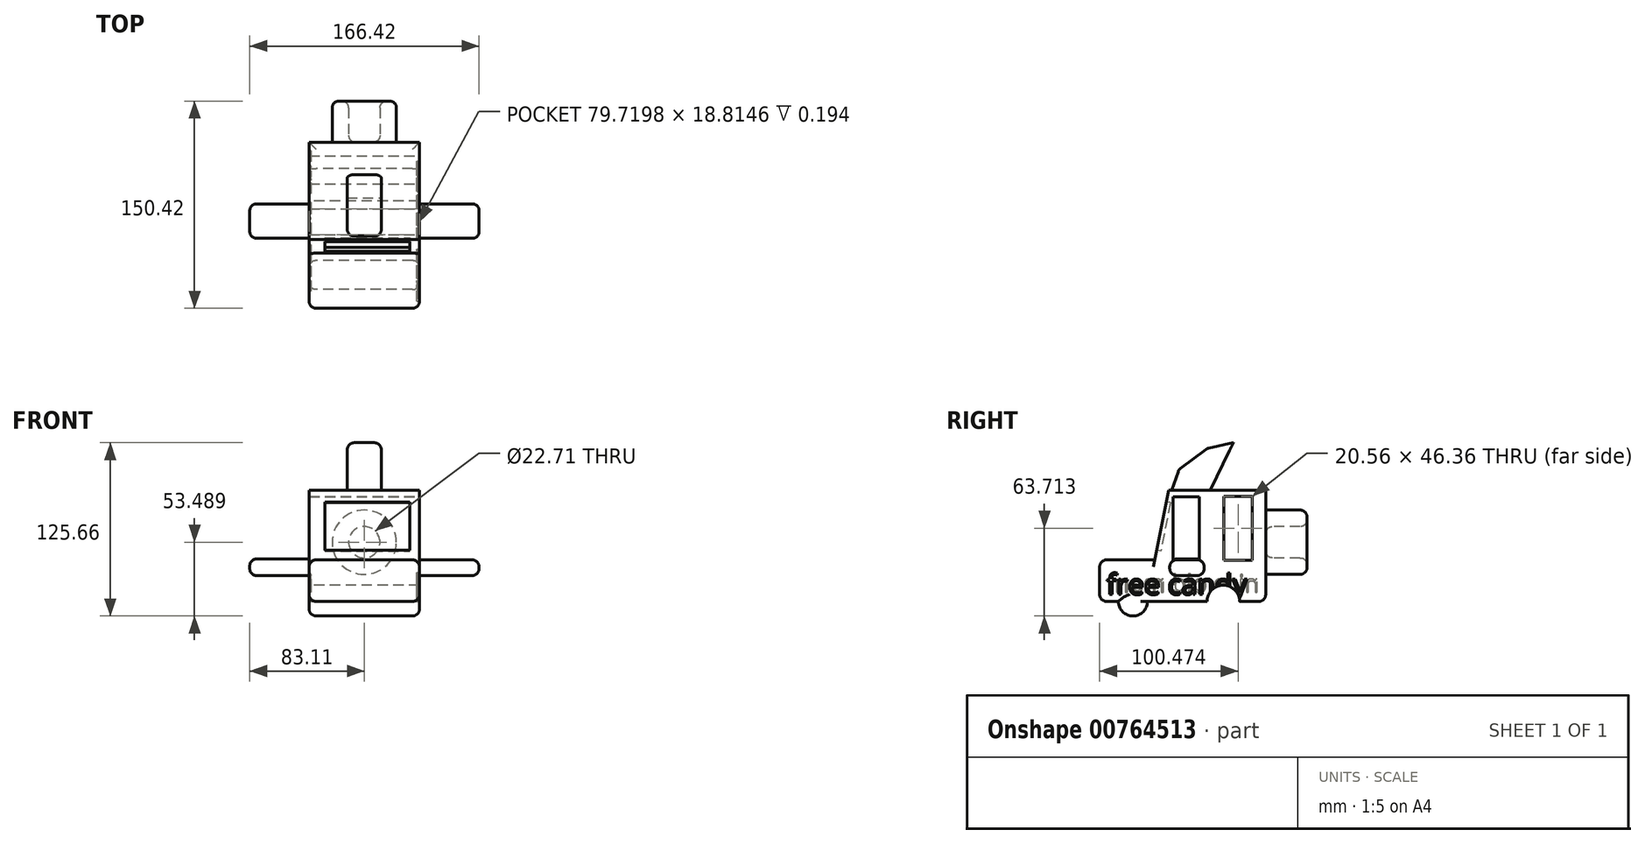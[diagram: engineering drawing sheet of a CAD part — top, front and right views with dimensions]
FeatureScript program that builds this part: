
annotation { "Feature Type Name" : "Feature", "Feature Type Description" : "" }
export const myFeature = defineFeature(function(context is Context, id is Id, definition is map)
    precondition{}
    {
        {
            var Q0;
            Q0=qCreatedBy(makeId("Right.planeOp"),FACE);
            var sketch = newSketch(context, id + "F0", { "sketchPlane" : qUnion([Q0])});
            skLineSegment(sketch, "E0", {"start": v(57.1, 32.48) * mm, "end": v(57.1, -48.17) * mm});
            skLineSegment(sketch, "E1", {"start": v(57.1, -48.17) * mm, "end": v(-63.33, -48.17) * mm});
            skLineSegment(sketch, "E2", {"start": v(-63.33, -48.17) * mm, "end": v(-63.33, -18) * mm});
            skLineSegment(sketch, "E3", {"start": v(-63.33, -18) * mm, "end": v(-23.28, -18) * mm});
            skLineSegment(sketch, "E4", {"start": v(57.1, 32.48) * mm, "end": v(-13.4, 32.48) * mm});
            skLineSegment(sketch, "E5", {"start": v(-13.4, 32.48) * mm, "end": v(-23.28, -18) * mm});
            skCircle(sketch, "E6", {"center": v(-39.2, -48.17) * mm, "radius": 10.5 * mm});
            skCircle(sketch, "E7", {"center": v(26.37, -48.17) * mm, "radius": 11.8 * mm});
            skSolve(sketch);
        }
        {
            var Q0;
            {var subQ5=sQuery(id+"F0.wireOp",EDGE,"E0");Q0=makeQuery(id+"F0.imprint","IMPRINT",FACE,{"disambiguationData":[TD([[makeQuery(id+"F0.imprint","IMPRINT",EDGE,{"derivedFrom":subQ5}),-1.0]])]});}
            extrude(context, id + "F1", {"entities" : qUnion([Q0]), "endBound" : BoundingType.SYMMETRIC, "depth" : 80 * mm, "offsetDistance" : 25 * mm});
        }
        {
            var Q0;
            {var subQ0=sQuery(id+"F0.wireOp",EDGE,"E6");var subQ1=sQuery(id+"F0.wireOp",EDGE,"E1");var subQ2=makeQuery(id+"F0.imprint","INTERSECT",VERTEX,{"disambiguationData":[OD(0.0)],"derivedFrom":[subQ1,subQ0]});Q0=makeQuery(id+"F0.imprint","IMPRINT",FACE,{"disambiguationData":[TD([[makeQuery(id+"F0.imprint","IMPRINT",EDGE,{"disambiguationData":[TD([[subQ2,-1.0]])],"derivedFrom":subQ1}),1.0]])]});}
            var Q1;
            {var subQ0=sQuery(id+"F0.wireOp",EDGE,"E6");var subQ1=sQuery(id+"F0.wireOp",EDGE,"E1");var subQ2=makeQuery(id+"F0.imprint","INTERSECT",VERTEX,{"disambiguationData":[OD(0.0)],"derivedFrom":[subQ1,subQ0]});Q1=makeQuery(id+"F0.imprint","IMPRINT",FACE,{"disambiguationData":[TD([[makeQuery(id+"F0.imprint","IMPRINT",EDGE,{"disambiguationData":[TD([[subQ2,-1.0]])],"derivedFrom":subQ1}),-1.0]])]});}
            var Q2;
            {var subQ0=sQuery(id+"F0.wireOp",EDGE,"E7");var subQ1=sQuery(id+"F0.wireOp",EDGE,"E1");var subQ2=makeQuery(id+"F0.imprint","INTERSECT",VERTEX,{"disambiguationData":[OD(0.0)],"derivedFrom":[subQ1,subQ0]});Q2=makeQuery(id+"F0.imprint","IMPRINT",FACE,{"disambiguationData":[TD([[makeQuery(id+"F0.imprint","IMPRINT",EDGE,{"disambiguationData":[TD([[subQ2,-1.0]])],"derivedFrom":subQ1}),1.0]])]});}
            var Q3;
            {var subQ0=sQuery(id+"F0.wireOp",EDGE,"E7");var subQ1=sQuery(id+"F0.wireOp",EDGE,"E1");var subQ2=makeQuery(id+"F0.imprint","INTERSECT",VERTEX,{"disambiguationData":[OD(0.0)],"derivedFrom":[subQ1,subQ0]});Q3=makeQuery(id+"F0.imprint","IMPRINT",FACE,{"disambiguationData":[TD([[makeQuery(id+"F0.imprint","IMPRINT",EDGE,{"disambiguationData":[TD([[subQ2,-1.0]])],"derivedFrom":subQ1}),-1.0]])]});}
            extrude(context, id + "F2", {"entities" : qUnion([Q0, Q1, Q2, Q3]), "operationType" : NewBodyOperationType.ADD, "endBound" : BoundingType.SYMMETRIC, "depth" : 80 * mm, "offsetDistance" : 25 * mm});
        }
        {
            var Q0;
            Q0=qCreatedBy(makeId("Right.planeOp"),FACE);
            var sketch = newSketch(context, id + "F3", { "sketchPlane" : qUnion([Q0])});
            skLineSegment(sketch, "E8.bottom", {"start": v(-9.99, 27.83) * mm, "end": v(8.83, 27.83) * mm});
            skLineSegment(sketch, "E8.top", {"start": v(-9.99, -18.14) * mm, "end": v(8.83, -18.14) * mm});
            skLineSegment(sketch, "E8.left", {"start": v(-9.99, 27.83) * mm, "end": v(-9.99, -18.14) * mm});
            skLineSegment(sketch, "E8.right", {"start": v(8.83, 27.83) * mm, "end": v(8.83, -18.14) * mm});
            skLineSegment(sketch, "E9.bottom", {"start": v(26.86, 28.22) * mm, "end": v(47.42, 28.22) * mm});
            skLineSegment(sketch, "E9.top", {"start": v(26.86, -18.14) * mm, "end": v(47.42, -18.14) * mm});
            skLineSegment(sketch, "E9.left", {"start": v(26.86, 28.22) * mm, "end": v(26.86, -18.14) * mm});
            skLineSegment(sketch, "E9.right", {"start": v(47.42, 28.22) * mm, "end": v(47.42, -18.14) * mm});
            skSolve(sketch);
        }
        {
            var Q0;
            Q0 = qSketchRegion(id + "F3", true);
            extrude(context, id + "F4", {"entities" : qUnion([Q0]), "operationType" : NewBodyOperationType.REMOVE, "endBound" : BoundingType.SYMMETRIC, "oppositeDirection" : true, "depth" : 80 * mm, "offsetDistance" : 25 * mm});
        }
        {
            var Q0;
            Q0=qCreatedBy(makeId("Front.planeOp"),FACE);
            var sketch = newSketch(context, id + "F5", { "sketchPlane" : qUnion([Q0])});
            skLineSegment(sketch, "E10.bottom", {"start": v(39.86, -17.94) * mm, "end": v(83.3, -17.94) * mm});
            skLineSegment(sketch, "E10.top", {"start": v(39.86, -29.39) * mm, "end": v(83.3, -29.39) * mm});
            skLineSegment(sketch, "E10.left", {"start": v(39.86, -17.94) * mm, "end": v(39.86, -29.39) * mm});
            skLineSegment(sketch, "E10.right", {"start": v(83.3, -17.94) * mm, "end": v(83.3, -29.39) * mm});
            skLineSegment(sketch, "E11.bottom", {"start": v(-39.86, -17.36) * mm, "end": v(-83.11, -17.36) * mm});
            skLineSegment(sketch, "E11.top", {"start": v(-39.86, -29.39) * mm, "end": v(-83.11, -29.39) * mm});
            skLineSegment(sketch, "E11.left", {"start": v(-39.86, -17.36) * mm, "end": v(-39.86, -29.39) * mm});
            skLineSegment(sketch, "E11.right", {"start": v(-83.11, -17.36) * mm, "end": v(-83.11, -29.39) * mm});
            skSolve(sketch);
        }
        {
            var Q0;
            Q0=makeQuery(id+"F5.imprint","IMPRINT",FACE,{"disambiguationData":[TD([[makeQuery(id+"F5.imprint","IMPRINT",EDGE,{"derivedFrom":sQuery(id+"F5.wireOp",EDGE,"E10.bottom")}),-1.0]])]});
            var Q1;
            Q1=makeQuery(id+"F5.imprint","IMPRINT",FACE,{"disambiguationData":[TD([[makeQuery(id+"F5.imprint","IMPRINT",EDGE,{"derivedFrom":sQuery(id+"F5.wireOp",EDGE,"E11.bottom")}),1.0]])]});
            extrude(context, id + "F6", {"entities" : qUnion([Q0, Q1]), "operationType" : NewBodyOperationType.ADD, "endBound" : BoundingType.SYMMETRIC, "depth" : 25 * mm, "offsetDistance" : 25 * mm});
        }
        {
            var Q0;
            Q0=makeQuery(id+"F6.opExtrude","SWEPT_EDGE",EDGE,{"disambiguationData":[OSD([sQuery(id+"F5.wireOp",EDGE,"E10.bottom"),sQuery(id+"F5.wireOp",EDGE,"E10.right")])]});
            var Q1;
            Q1=makeQuery(id+"F6.opExtrude","CAP_EDGE",EDGE,{"disambiguationData":[OSD([sQuery(id+"F5.wireOp",EDGE,"E10.right")])],"isStart":false});
            var Q2;
            Q2=makeQuery(id+"F6.opExtrude","SWEPT_EDGE",EDGE,{"disambiguationData":[OSD([sQuery(id+"F5.wireOp",EDGE,"E10.top"),sQuery(id+"F5.wireOp",EDGE,"E10.right")])]});
            var Q3;
            Q3=makeQuery(id+"F6.opExtrude","CAP_EDGE",EDGE,{"disambiguationData":[OSD([sQuery(id+"F5.wireOp",EDGE,"E10.right")])],"isStart":true});
            var Q4;
            Q4=makeQuery(id+"F6.opExtrude","CAP_EDGE",EDGE,{"disambiguationData":[OSD([sQuery(id+"F5.wireOp",EDGE,"E10.bottom")])],"isStart":true});
            var Q5;
            Q5=makeQuery(id+"F6.opExtrude","CAP_EDGE",EDGE,{"disambiguationData":[OSD([sQuery(id+"F5.wireOp",EDGE,"E10.top")])],"isStart":true});
            var Q6;
            Q6=makeQuery(id+"F6.opExtrude","CAP_EDGE",EDGE,{"disambiguationData":[OSD([sQuery(id+"F5.wireOp",EDGE,"E10.bottom")])],"isStart":false});
            var Q7;
            Q7=makeQuery(id+"F6.opExtrude","CAP_EDGE",EDGE,{"disambiguationData":[OSD([sQuery(id+"F5.wireOp",EDGE,"E10.top")])],"isStart":false});
            var Q8;
            Q8=makeQuery(id+"F6.opExtrude","SWEPT_EDGE",EDGE,{"disambiguationData":[OSD([sQuery(id+"F5.wireOp",EDGE,"E11.bottom"),sQuery(id+"F5.wireOp",EDGE,"E11.right")])]});
            var Q9;
            Q9=makeQuery(id+"F6.opExtrude","SWEPT_EDGE",EDGE,{"disambiguationData":[OSD([sQuery(id+"F5.wireOp",EDGE,"E11.top"),sQuery(id+"F5.wireOp",EDGE,"E11.right")])]});
            var Q10;
            Q10=makeQuery(id+"F6.opExtrude","CAP_EDGE",EDGE,{"disambiguationData":[OSD([sQuery(id+"F5.wireOp",EDGE,"E11.right")])],"isStart":true});
            var Q11;
            Q11=makeQuery(id+"F6.opExtrude","CAP_EDGE",EDGE,{"disambiguationData":[OSD([sQuery(id+"F5.wireOp",EDGE,"E11.right")])],"isStart":false});
            var Q12;
            Q12=makeQuery(id+"F6.opExtrude","CAP_EDGE",EDGE,{"disambiguationData":[OSD([sQuery(id+"F5.wireOp",EDGE,"E11.bottom")])],"isStart":true});
            var Q13;
            Q13=makeQuery(id+"F6.opExtrude","CAP_EDGE",EDGE,{"disambiguationData":[OSD([sQuery(id+"F5.wireOp",EDGE,"E11.top")])],"isStart":true});
            var Q14;
            Q14=makeQuery(id+"F6.opExtrude","CAP_EDGE",EDGE,{"disambiguationData":[OSD([sQuery(id+"F5.wireOp",EDGE,"E11.bottom")])],"isStart":false});
            var Q15;
            Q15=makeQuery(id+"F6.opExtrude","CAP_EDGE",EDGE,{"disambiguationData":[OSD([sQuery(id+"F5.wireOp",EDGE,"E11.top")])],"isStart":false});
            fillet(context, id + "F7", {"entities" : qUnion([Q0, Q1, Q2, Q3, Q4, Q5, Q6, Q7, Q8, Q9, Q10, Q11, Q12, Q13, Q14, Q15]), "radius" : 5 * mm, "tangentPropagation" : true, "allowEdgeOverflow" : false});
        }
        {
            var Q0;
            Q0=makeQuery(id+"F1.opExtrude","SWEPT_FACE",FACE,{"disambiguationData":[OSD([sQuery(id+"F0.wireOp",EDGE,"E0")])]});
            var sketch = newSketch(context, id + "F8", { "sketchPlane" : qUnion([Q0])});
            skCircle(sketch, "E12", {"center": v(0, -5.18) * mm, "radius": 23.31 * mm});
            skCircle(sketch, "E13", {"center": v(0, -5.18) * mm, "radius": 11.35 * mm});
            skSolve(sketch);
        }
        {
            var Q0;
            Q0=makeQuery(id+"F8.imprint","IMPRINT",FACE,{"disambiguationData":[TD([[makeQuery(id+"F8.imprint","IMPRINT",EDGE,{"derivedFrom":sQuery(id+"F8.wireOp",EDGE,"E12")}),1.0]])]});
            extrude(context, id + "F9", {"entities" : qUnion([Q0]), "operationType" : NewBodyOperationType.ADD, "depth" : 30 * mm, "offsetDistance" : 25 * mm});
        }
        {
            var Q0;
            Q0=makeQuery(id+"F9.opExtrude","CAP_EDGE",EDGE,{"disambiguationData":[OSD([sQuery(id+"F8.wireOp",EDGE,"E13")])],"isStart":false});
            var Q1;
            Q1=makeQuery(id+"F9.opExtrude","CAP_EDGE",EDGE,{"disambiguationData":[OSD([sQuery(id+"F8.wireOp",EDGE,"E13")])],"isStart":true});
            var Q2;
            Q2=makeQuery(id+"F9.opExtrude","CAP_EDGE",EDGE,{"disambiguationData":[OSD([sQuery(id+"F8.wireOp",EDGE,"E12")])],"isStart":false});
            fillet(context, id + "F10", {"entities" : qUnion([Q0, Q1, Q2]), "radius" : 5 * mm, "tangentPropagation" : true, "allowEdgeOverflow" : false});
        }
        {
            var Q0;
            Q0=qCreatedBy(makeId("Right.planeOp"),FACE);
            var sketch = newSketch(context, id + "F11", { "sketchPlane" : qUnion([Q0])});
            skLineSegment(sketch, "E14", {"start": v(-11.68, 30.27) * mm, "end": v(-5.95, 47.44) * mm});
            skLineSegment(sketch, "E15", {"start": v(-5.95, 47.44) * mm, "end": v(14.65, 62.83) * mm});
            skLineSegment(sketch, "E16", {"start": v(14.65, 62.83) * mm, "end": v(33.65, 67) * mm});
            skLineSegment(sketch, "E17", {"start": v(33.65, 67) * mm, "end": v(15.84, 30.18) * mm});
            skLineSegment(sketch, "E18", {"start": v(-11.68, 30.27) * mm, "end": v(15.84, 30.18) * mm});
            skSolve(sketch);
        }
        {
            var Q0;
            Q0=makeQuery(id+"F11.imprint","IMPRINT",FACE,{"disambiguationData":[TD([[makeQuery(id+"F11.imprint","IMPRINT",EDGE,{"derivedFrom":sQuery(id+"F11.wireOp",EDGE,"E14")}),-1.0]])]});
            extrude(context, id + "F12", {"entities" : qUnion([Q0]), "operationType" : NewBodyOperationType.ADD, "endBound" : BoundingType.SYMMETRIC, "depth" : 25 * mm, "offsetDistance" : 25 * mm});
        }
        {
            var Q0;
            Q0=makeQuery(id+"F12.opExtrude","SWEPT_EDGE",EDGE,{"disambiguationData":[OSD([sQuery(id+"F11.wireOp",EDGE,"E14"),sQuery(id+"F11.wireOp",EDGE,"E15")])]});
            var Q1;
            Q1=makeQuery(id+"F12.opExtrude","SWEPT_EDGE",EDGE,{"disambiguationData":[OSD([sQuery(id+"F11.wireOp",EDGE,"E15"),sQuery(id+"F11.wireOp",EDGE,"E16")])]});
            var Q2;
            Q2=makeQuery(id+"F12.opExtrude","CAP_EDGE",EDGE,{"disambiguationData":[OSD([sQuery(id+"F11.wireOp",EDGE,"E14")])],"isStart":false});
            var Q3;
            Q3=makeQuery(id+"F12.opExtrude","CAP_EDGE",EDGE,{"disambiguationData":[OSD([sQuery(id+"F11.wireOp",EDGE,"E14")])],"isStart":true});
            var Q4;
            Q4=makeQuery(id+"F12.opExtrude","CAP_EDGE",EDGE,{"disambiguationData":[OSD([sQuery(id+"F11.wireOp",EDGE,"E15")])],"isStart":false});
            var Q5;
            Q5=makeQuery(id+"F12.opExtrude","CAP_EDGE",EDGE,{"disambiguationData":[OSD([sQuery(id+"F11.wireOp",EDGE,"E15")])],"isStart":true});
            var Q6;
            Q6=makeQuery(id+"F12.opExtrude","CAP_EDGE",EDGE,{"disambiguationData":[OSD([sQuery(id+"F11.wireOp",EDGE,"E16")])],"isStart":false});
            var Q7;
            Q7=makeQuery(id+"F12.opExtrude","CAP_EDGE",EDGE,{"disambiguationData":[OSD([sQuery(id+"F11.wireOp",EDGE,"E16")])],"isStart":true});
            fillet(context, id + "F13", {"entities" : qUnion([Q0, Q1, Q2, Q3, Q4, Q5, Q6, Q7]), "radius" : 5 * mm, "tangentPropagation" : true, "allowEdgeOverflow" : false});
        }
        {
            var Q0;
            Q0=makeQuery(id+"F1.opExtrude","SWEPT_FACE",FACE,{"disambiguationData":[OSD([sQuery(id+"F0.wireOp",EDGE,"E5")])]});
            var sketch = newSketch(context, id + "F14", { "sketchPlane" : qUnion([Q0])});
            skLineSegment(sketch, "E19.bottom", {"start": v(-28.65, 20.74) * mm, "end": v(33.12, 20.74) * mm});
            skLineSegment(sketch, "E19.top", {"start": v(-28.65, -14.87) * mm, "end": v(33.12, -14.87) * mm});
            skLineSegment(sketch, "E19.left", {"start": v(-28.65, 20.74) * mm, "end": v(-28.65, -14.87) * mm});
            skLineSegment(sketch, "E19.right", {"start": v(33.12, 20.74) * mm, "end": v(33.12, -14.87) * mm});
            skSolve(sketch);
        }
        {
            var Q0;
            Q0=makeQuery(id+"F14.imprint","IMPRINT",FACE,{"disambiguationData":[TD([[makeQuery(id+"F14.imprint","IMPRINT",EDGE,{"derivedFrom":sQuery(id+"F14.wireOp",EDGE,"E19.bottom")}),-1.0]])]});
            extrude(context, id + "F15", {"entities" : qUnion([Q0]), "operationType" : NewBodyOperationType.REMOVE, "oppositeDirection" : true, "depth" : 3 * mm, "offsetDistance" : 25 * mm});
        }
        {
            var Q0;
            Q0=makeQuery(id+"F1.opExtrude","SWEPT_EDGE",EDGE,{"disambiguationData":[OSD([sQuery(id+"F0.wireOp",EDGE,"E2"),sQuery(id+"F0.wireOp",EDGE,"E3")])]});
            var Q1;
            Q1=makeQuery(id+"F1.opExtrude","CAP_EDGE",EDGE,{"disambiguationData":[OSD([sQuery(id+"F0.wireOp",EDGE,"E2")])],"isStart":false});
            var Q2;
            Q2=makeQuery(id+"F1.opExtrude","CAP_EDGE",EDGE,{"disambiguationData":[OSD([sQuery(id+"F0.wireOp",EDGE,"E2")])],"isStart":true});
            var Q3;
            Q3=makeQuery(id+"F1.opExtrude","SWEPT_EDGE",EDGE,{"disambiguationData":[OSD([sQuery(id+"F0.wireOp",EDGE,"E1"),sQuery(id+"F0.wireOp",EDGE,"E2")])]});
            var Q4;
            {var subQ0=sQuery(id+"F0.wireOp",EDGE,"E1");Q4=makeQuery(id+"F1.opExtrude","CAP_EDGE",EDGE,{"disambiguationData":[OSD([subQ0]),TDD([makeQuery(id+"F0.imprint","IMPRINT",EDGE,{"disambiguationData":[TD([[makeQuery(id+"F0.imprint","INTERSECT",VERTEX,{"derivedFrom":[subQ0,sQuery(id+"F0.wireOp",EDGE,"E2")]}),1.0]])],"derivedFrom":subQ0})])],"isStart":false});}
            var Q5;
            Q5=makeQuery(id+"F2.opExtrude","CAP_EDGE",EDGE,{"disambiguationData":[OSD([sQuery(id+"F0.wireOp",EDGE,"E6")])],"isStart":false});
            var Q6;
            {var subQ0=sQuery(id+"F0.wireOp",EDGE,"E1");Q6=makeQuery(id+"F1.opExtrude","CAP_EDGE",EDGE,{"disambiguationData":[OSD([subQ0]),TDD([makeQuery(id+"F0.imprint","IMPRINT",EDGE,{"disambiguationData":[TD([[makeQuery(id+"F0.imprint","INTERSECT",VERTEX,{"disambiguationData":[OD(1.0)],"derivedFrom":[subQ0,sQuery(id+"F0.wireOp",EDGE,"E7")]}),-1.0]])],"derivedFrom":subQ0})])],"isStart":false});}
            var Q7;
            Q7=makeQuery(id+"F2.opExtrude","CAP_EDGE",EDGE,{"disambiguationData":[OSD([sQuery(id+"F0.wireOp",EDGE,"E7")])],"isStart":false});
            var Q8;
            {var subQ0=sQuery(id+"F0.wireOp",EDGE,"E1");Q8=makeQuery(id+"F1.opExtrude","CAP_EDGE",EDGE,{"disambiguationData":[OSD([subQ0]),TDD([makeQuery(id+"F0.imprint","IMPRINT",EDGE,{"disambiguationData":[TD([[makeQuery(id+"F0.imprint","INTERSECT",VERTEX,{"derivedFrom":[sQuery(id+"F0.wireOp",EDGE,"E0"),subQ0]}),-1.0]])],"derivedFrom":subQ0})])],"isStart":false});}
            var Q9;
            Q9=makeQuery(id+"F1.opExtrude","SWEPT_EDGE",EDGE,{"disambiguationData":[OSD([sQuery(id+"F0.wireOp",EDGE,"E0"),sQuery(id+"F0.wireOp",EDGE,"E1")])]});
            var Q10;
            {var subQ0=sQuery(id+"F0.wireOp",EDGE,"E1");Q10=makeQuery(id+"F1.opExtrude","CAP_EDGE",EDGE,{"disambiguationData":[OSD([subQ0]),TDD([makeQuery(id+"F0.imprint","IMPRINT",EDGE,{"disambiguationData":[TD([[makeQuery(id+"F0.imprint","INTERSECT",VERTEX,{"derivedFrom":[sQuery(id+"F0.wireOp",EDGE,"E0"),subQ0]}),-1.0]])],"derivedFrom":subQ0})])],"isStart":true});}
            var Q11;
            Q11=makeQuery(id+"F2.opExtrude","CAP_EDGE",EDGE,{"disambiguationData":[OSD([sQuery(id+"F0.wireOp",EDGE,"E7")])],"isStart":true});
            var Q12;
            {var subQ0=sQuery(id+"F0.wireOp",EDGE,"E1");Q12=makeQuery(id+"F1.opExtrude","CAP_EDGE",EDGE,{"disambiguationData":[OSD([subQ0]),TDD([makeQuery(id+"F0.imprint","IMPRINT",EDGE,{"disambiguationData":[TD([[makeQuery(id+"F0.imprint","INTERSECT",VERTEX,{"disambiguationData":[OD(1.0)],"derivedFrom":[subQ0,sQuery(id+"F0.wireOp",EDGE,"E7")]}),-1.0]])],"derivedFrom":subQ0})])],"isStart":true});}
            var Q13;
            Q13=makeQuery(id+"F2.opExtrude","CAP_EDGE",EDGE,{"disambiguationData":[OSD([sQuery(id+"F0.wireOp",EDGE,"E6")])],"isStart":true});
            var Q14;
            {var subQ0=sQuery(id+"F0.wireOp",EDGE,"E1");Q14=makeQuery(id+"F1.opExtrude","CAP_EDGE",EDGE,{"disambiguationData":[OSD([subQ0]),TDD([makeQuery(id+"F0.imprint","IMPRINT",EDGE,{"disambiguationData":[TD([[makeQuery(id+"F0.imprint","INTERSECT",VERTEX,{"derivedFrom":[subQ0,sQuery(id+"F0.wireOp",EDGE,"E2")]}),1.0]])],"derivedFrom":subQ0})])],"isStart":true});}
            fillet(context, id + "F16", {"entities" : qUnion([Q0, Q1, Q2, Q3, Q4, Q5, Q6, Q7, Q8, Q9, Q10, Q11, Q12, Q13, Q14]), "radius" : 5 * mm, "tangentPropagation" : true, "allowEdgeOverflow" : false});
        }
        {
            var Q0;
            Q0=makeQuery(id+"F1.opExtrude","CAP_EDGE",EDGE,{"disambiguationData":[OSD([sQuery(id+"F0.wireOp",EDGE,"E3")])],"isStart":true});
            var Q1;
            Q1=makeQuery(id+"F1.opExtrude","CAP_EDGE",EDGE,{"disambiguationData":[OSD([sQuery(id+"F0.wireOp",EDGE,"E3")])],"isStart":false});
            fillet(context, id + "F17", {"entities" : qUnion([Q0, Q1]), "radius" : 5 * mm, "tangentPropagation" : true, "allowEdgeOverflow" : false});
        }
        {
            var Q0;
            {var subQ0=sQuery(id+"F0.wireOp",EDGE,"E7");var subQ1=sQuery(id+"F0.wireOp",EDGE,"E6");Q0=makeQuery(id+"F2.boolean.opBoolean","MERGE",FACE,{"derivedFrom":[makeQuery(id+"F1.opExtrude","CAP_FACE",FACE,{"disambiguationData":[OSD([sQuery(id+"F0.wireOp",EDGE,"E0"),sQuery(id+"F0.wireOp",EDGE,"E1"),sQuery(id+"F0.wireOp",EDGE,"E2"),sQuery(id+"F0.wireOp",EDGE,"E3"),sQuery(id+"F0.wireOp",EDGE,"E4"),sQuery(id+"F0.wireOp",EDGE,"E5"),subQ1,subQ0])],"isStart":false}),makeQuery(id+"F2.opExtrude","CAP_FACE",FACE,{"disambiguationData":[OSD([subQ1])],"isStart":false}),makeQuery(id+"F2.opExtrude","CAP_FACE",FACE,{"disambiguationData":[OSD([subQ0])],"isStart":false})]});}
            var sketch = newSketch(context, id + "F18", { "sketchPlane" : qUnion([Q0])});
            skText(sketch, "E20", { "text": "free candy", "fontName": "OpenSans-Regular.ttf"});
            const initialGuessF18  = {"E20": [-0.05833, -0.04317, 1, 0, 0.015]};
            skSetInitialGuess(sketch, initialGuessF18);
            skSolve(sketch);
        }
        {
            var Q0;
            Q0 = qSketchRegion(id + "F18", true);
            extrude(context, id + "F19", {"entities" : qUnion([Q0]), "operationType" : NewBodyOperationType.REMOVE, "oppositeDirection" : true, "depth" : 2 * mm, "offsetDistance" : 25 * mm});
        }
        {
            var Q0;
            {var subQ0=sQuery(id+"F0.wireOp",EDGE,"E7");var subQ1=sQuery(id+"F0.wireOp",EDGE,"E6");Q0=makeQuery(id+"F2.boolean.opBoolean","MERGE",FACE,{"derivedFrom":[makeQuery(id+"F1.opExtrude","CAP_FACE",FACE,{"disambiguationData":[OSD([sQuery(id+"F0.wireOp",EDGE,"E0"),sQuery(id+"F0.wireOp",EDGE,"E1"),sQuery(id+"F0.wireOp",EDGE,"E2"),sQuery(id+"F0.wireOp",EDGE,"E3"),sQuery(id+"F0.wireOp",EDGE,"E4"),sQuery(id+"F0.wireOp",EDGE,"E5"),subQ1,subQ0])],"isStart":true}),makeQuery(id+"F2.opExtrude","CAP_FACE",FACE,{"disambiguationData":[OSD([subQ1])],"isStart":true}),makeQuery(id+"F2.opExtrude","CAP_FACE",FACE,{"disambiguationData":[OSD([subQ0])],"isStart":true})]});}
            var sketch = newSketch(context, id + "F20", { "sketchPlane" : qUnion([Q0])});
            skText(sketch, "E21", { "text": "nice old man", "fontName": "OpenSans-Regular.ttf"});
            const initialGuessF20  = {"E21": [-0.0525, -0.04141, 1, 0, 0.0126]};
            skSetInitialGuess(sketch, initialGuessF20);
            skSolve(sketch);
        }
        {
            var Q0;
            Q0 = qSketchRegion(id + "F20", true);
            extrude(context, id + "F21", {"entities" : qUnion([Q0]), "operationType" : NewBodyOperationType.REMOVE, "oppositeDirection" : true, "depth" : 1.2 * mm, "offsetDistance" : 25 * mm});
        }
    });
